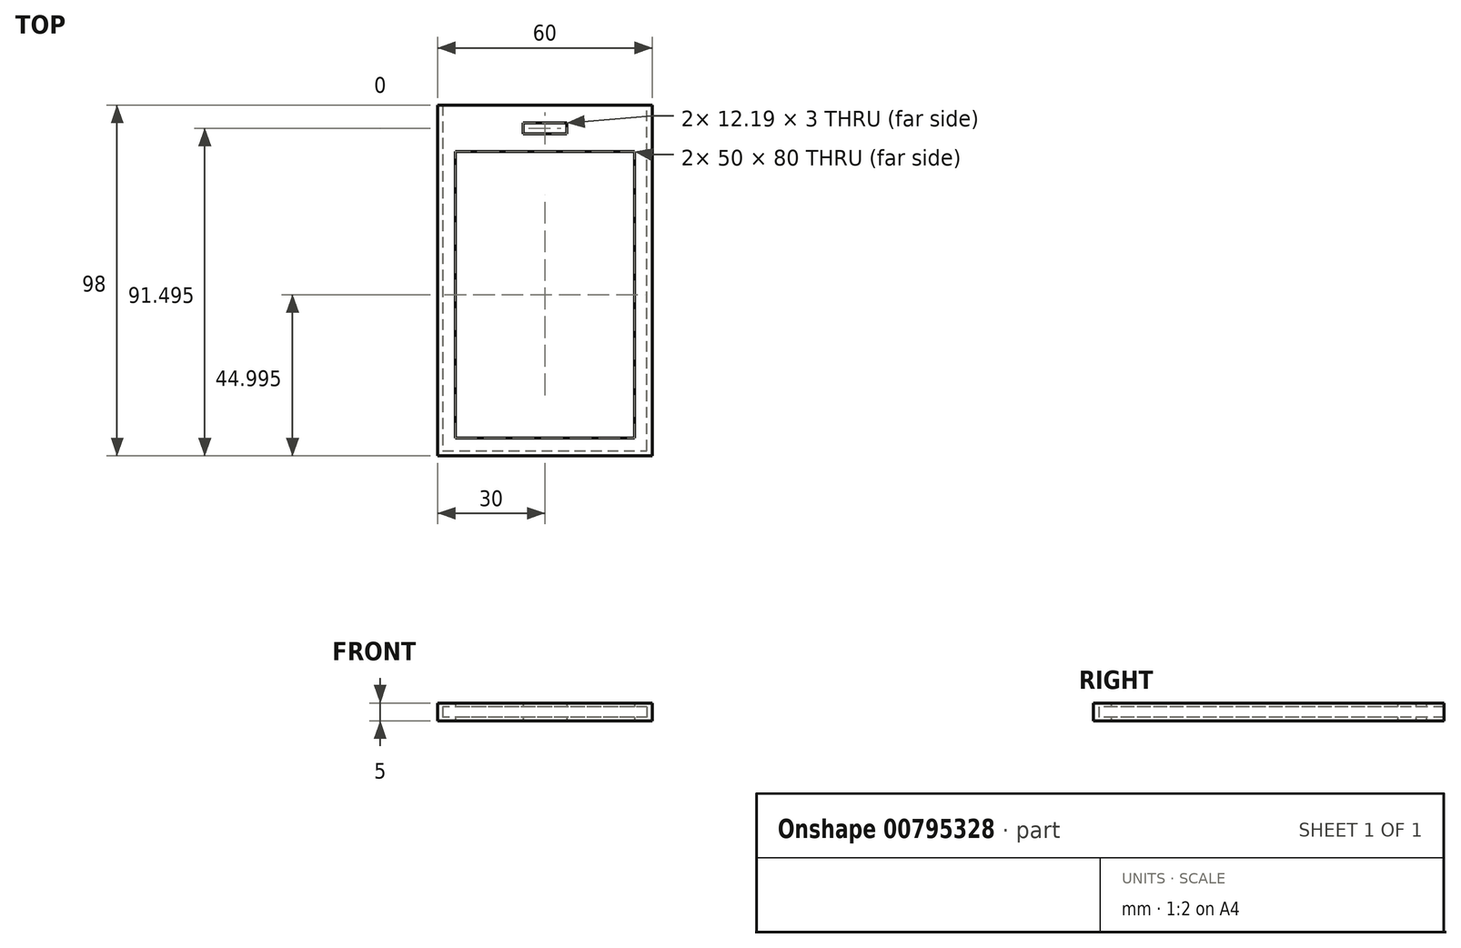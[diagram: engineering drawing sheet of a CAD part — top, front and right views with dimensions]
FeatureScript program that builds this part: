
annotation { "Feature Type Name" : "Feature", "Feature Type Description" : "" }
export const myFeature = defineFeature(function(context is Context, id is Id, definition is map)
    precondition{}
    {
        {
            var Q0;
            Q0=qCreatedBy(makeId("Top.planeOp"),FACE);
            var sketch = newSketch(context, id + "F0", { "sketchPlane" : qUnion([Q0])});
            skLineSegment(sketch, "E0.bottom", {"start": v(30, 55.46) * mm, "end": v(-30, 55.46) * mm});
            skLineSegment(sketch, "E0.top", {"start": v(30, -42.54) * mm, "end": v(-30, -42.54) * mm});
            skLineSegment(sketch, "E0.left", {"start": v(30, 55.46) * mm, "end": v(30, -42.54) * mm});
            skLineSegment(sketch, "E0.right", {"start": v(-30, 55.46) * mm, "end": v(-30, -42.54) * mm});
            skPoint(sketch, "E0.middle", {"position": v(0, 0) * mm});
            skLineSegment(sketch, "E1.bottom", {"start": v(25, 42.46) * mm, "end": v(-25, 42.46) * mm});
            skLineSegment(sketch, "E1.top", {"start": v(25, -37.54) * mm, "end": v(-25, -37.54) * mm});
            skLineSegment(sketch, "E1.left", {"start": v(25, 42.46) * mm, "end": v(25, -37.54) * mm});
            skLineSegment(sketch, "E1.right", {"start": v(-25, 42.46) * mm, "end": v(-25, -37.54) * mm});
            skLineSegment(sketch, "E2.bottom", {"start": v(6.1, 50.46) * mm, "end": v(-6.1, 50.46) * mm});
            skLineSegment(sketch, "E2.top", {"start": v(6.1, 47.46) * mm, "end": v(-6.1, 47.46) * mm});
            skLineSegment(sketch, "E2.left", {"start": v(6.1, 50.46) * mm, "end": v(6.1, 47.46) * mm});
            skLineSegment(sketch, "E2.right", {"start": v(-6.1, 50.46) * mm, "end": v(-6.1, 47.46) * mm});
            skPoint(sketch, "E2.middle", {"position": v(0, 48.96) * mm});
            skPoint(sketch, "E2.middle.positionSnap0", {"position": v(0, 55.46) * mm});
            skPoint(sketch, "E2.centerSnap0", {"position": v(0, 55.46) * mm});
            skSolve(sketch);
        }
        {
            var Q0;
            Q0=makeQuery(id+"F0.imprint","IMPRINT",FACE,{"disambiguationData":[TD([[makeQuery(id+"F0.imprint","IMPRINT",EDGE,{"derivedFrom":sQuery(id+"F0.wireOp",EDGE,"E0.bottom")}),1.0]])]});
            extrude(context, id + "F1", {"entities" : qUnion([Q0]), "depth" : 1 * mm, "offsetDistance" : 25 * mm});
        }
        {
            var Q0;
            Q0=makeQuery(id+"F1.opExtrude","CAP_FACE",FACE,{"disambiguationData":[OSD([sQuery(id+"F0.wireOp",EDGE,"E0.bottom"),sQuery(id+"F0.wireOp",EDGE,"E0.top"),sQuery(id+"F0.wireOp",EDGE,"E0.left"),sQuery(id+"F0.wireOp",EDGE,"E0.right"),sQuery(id+"F0.wireOp",EDGE,"E1.bottom"),sQuery(id+"F0.wireOp",EDGE,"E1.top"),sQuery(id+"F0.wireOp",EDGE,"E1.left"),sQuery(id+"F0.wireOp",EDGE,"E1.right"),sQuery(id+"F0.wireOp",EDGE,"E2.bottom"),sQuery(id+"F0.wireOp",EDGE,"E2.top"),sQuery(id+"F0.wireOp",EDGE,"E2.left"),sQuery(id+"F0.wireOp",EDGE,"E2.right")])],"isStart":false});
            var sketch = newSketch(context, id + "F2", { "sketchPlane" : qUnion([Q0])});
            skLineSegment(sketch, "E3", {"start": v(-30, 55.46) * mm, "end": v(-28.5, 55.46) * mm});
            skLineSegment(sketch, "E4", {"start": v(-28.5, 55.46) * mm, "end": v(-28.5, -41.04) * mm});
            skLineSegment(sketch, "E5", {"start": v(-28.5, -41.04) * mm, "end": v(28.5, -41.04) * mm});
            skLineSegment(sketch, "E6", {"start": v(28.5, -41.04) * mm, "end": v(28.5, 55.46) * mm});
            skLineSegment(sketch, "E7", {"start": v(28.5, 55.46) * mm, "end": v(30, 55.46) * mm});
            skLineSegment(sketch, "E8", {"start": v(30, 55.46) * mm, "end": v(30, -42.54) * mm});
            skLineSegment(sketch, "E9", {"start": v(30, -42.54) * mm, "end": v(-30, -42.54) * mm});
            skLineSegment(sketch, "E10", {"start": v(-30, -42.54) * mm, "end": v(-30, 55.46) * mm});
            skSolve(sketch);
        }
        {
            var Q0;
            Q0=makeQuery(id+"F2.imprint","IMPRINT",FACE,{"disambiguationData":[TD([[makeQuery(id+"F2.imprint","IMPRINT",EDGE,{"derivedFrom":sQuery(id+"F2.wireOp",EDGE,"E3")}),1.0]])]});
            extrude(context, id + "F3", {"entities" : qUnion([Q0]), "operationType" : NewBodyOperationType.ADD, "depth" : 3 * mm, "offsetDistance" : 25 * mm});
        }
        {
            var Q0;
            Q0=makeQuery(id+"F3.opExtrude","CAP_FACE",FACE,{"disambiguationData":[OSD([sQuery(id+"F2.wireOp",EDGE,"E3"),sQuery(id+"F2.wireOp",EDGE,"E4"),sQuery(id+"F2.wireOp",EDGE,"E5"),sQuery(id+"F2.wireOp",EDGE,"E6"),sQuery(id+"F2.wireOp",EDGE,"E7"),sQuery(id+"F2.wireOp",EDGE,"E8"),sQuery(id+"F2.wireOp",EDGE,"E9"),sQuery(id+"F2.wireOp",EDGE,"E10")])],"isStart":false});
            var sketch = newSketch(context, id + "F4", { "sketchPlane" : qUnion([Q0])});
            skLineSegment(sketch, "E11.bottom", {"start": v(30, 55.46) * mm, "end": v(-30, 55.46) * mm});
            skLineSegment(sketch, "E11.top", {"start": v(30, -42.54) * mm, "end": v(-30, -42.54) * mm});
            skLineSegment(sketch, "E11.left", {"start": v(30, 55.46) * mm, "end": v(30, -42.54) * mm});
            skLineSegment(sketch, "E11.right", {"start": v(-30, 55.46) * mm, "end": v(-30, -42.54) * mm});
            skPoint(sketch, "E11.middle", {"position": v(0, 0) * mm});
            skLineSegment(sketch, "E12.bottom", {"start": v(25, 42.46) * mm, "end": v(-25, 42.46) * mm});
            skLineSegment(sketch, "E12.top", {"start": v(25, -37.54) * mm, "end": v(-25, -37.54) * mm});
            skLineSegment(sketch, "E12.left", {"start": v(25, 42.46) * mm, "end": v(25, -37.54) * mm});
            skLineSegment(sketch, "E12.right", {"start": v(-25, 42.46) * mm, "end": v(-25, -37.54) * mm});
            skLineSegment(sketch, "E13.bottom", {"start": v(6.1, 50.46) * mm, "end": v(-6.1, 50.46) * mm});
            skLineSegment(sketch, "E13.top", {"start": v(6.1, 47.46) * mm, "end": v(-6.1, 47.46) * mm});
            skLineSegment(sketch, "E13.left", {"start": v(6.1, 50.46) * mm, "end": v(6.1, 47.46) * mm});
            skLineSegment(sketch, "E13.right", {"start": v(-6.1, 50.46) * mm, "end": v(-6.1, 47.46) * mm});
            skPoint(sketch, "E13.middle", {"position": v(0, 48.96) * mm});
            skPoint(sketch, "E13.middle.positionSnap0", {"position": v(0, 55.46) * mm});
            skPoint(sketch, "E13.centerSnap0", {"position": v(0, 55.46) * mm});
            skSolve(sketch);
        }
        {
            var Q0;
            Q0=makeQuery(id+"F4.imprint","IMPRINT",FACE,{"disambiguationData":[TD([[makeQuery(id+"F4.imprint","IMPRINT",EDGE,{"derivedFrom":sQuery(id+"F4.wireOp",EDGE,"E12.bottom")}),-1.0]])]});
            var Q1;
            Q1=makeQuery(id+"F4.imprint","IMPRINT",FACE,{"disambiguationData":[TD([[makeQuery(id+"F4.imprint","IMPRINT",EDGE,{"derivedFrom":sQuery(id+"F4.wireOp",EDGE,"E11.top")}),-1.0]])]});
            extrude(context, id + "F5", {"entities" : qUnion([Q0, Q1]), "operationType" : NewBodyOperationType.ADD, "depth" : 1 * mm, "offsetDistance" : 25 * mm});
        }
    });
